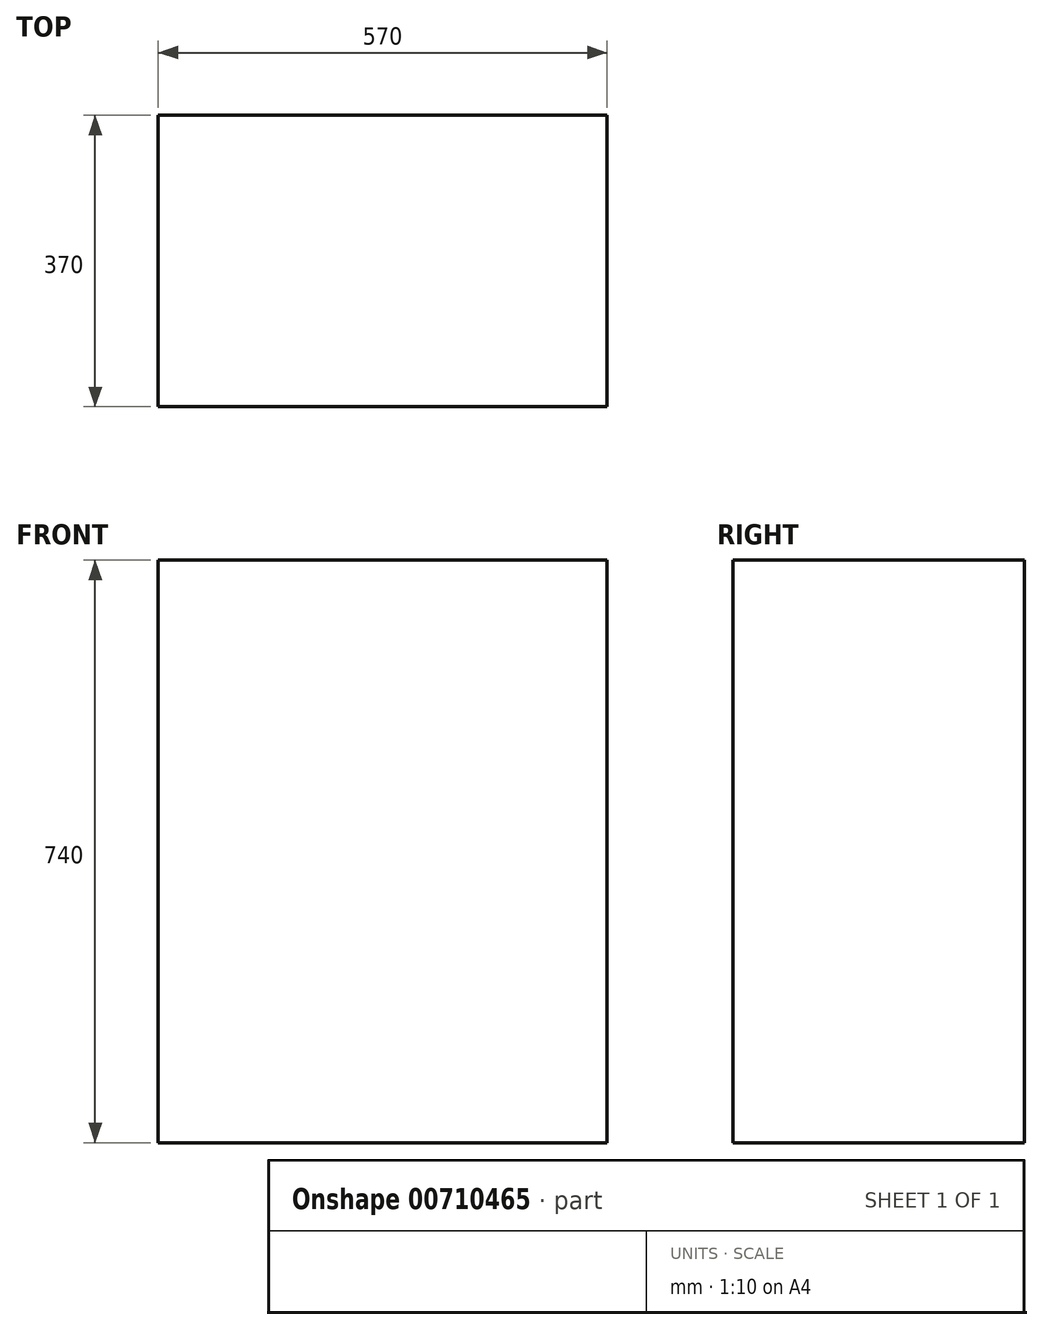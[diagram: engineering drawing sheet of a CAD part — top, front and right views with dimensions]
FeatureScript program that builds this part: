
annotation { "Feature Type Name" : "Feature", "Feature Type Description" : "" }
export const myFeature = defineFeature(function(context is Context, id is Id, definition is map)
    precondition{}
    {
        {
            var Q0;
            Q0=qCreatedBy(makeId("Top.planeOp"),FACE);
            var sketch = newSketch(context, id + "F0", { "sketchPlane" : qUnion([Q0])});
            skLineSegment(sketch, "E0.bottom", {"start": v(285, 185) * mm, "end": v(-285, 185) * mm});
            skLineSegment(sketch, "E0.top", {"start": v(285, -185) * mm, "end": v(-285, -185) * mm});
            skLineSegment(sketch, "E0.left", {"start": v(285, 185) * mm, "end": v(285, -185) * mm});
            skLineSegment(sketch, "E0.right", {"start": v(-285, 185) * mm, "end": v(-285, -185) * mm});
            skPoint(sketch, "E0.middle", {"position": v(0, 0) * mm});
            skSolve(sketch);
        }
        {
            var Q0;
            Q0=makeQuery(id+"F0.imprint","IMPRINT",FACE,{"disambiguationData":[TD([[makeQuery(id+"F0.imprint","IMPRINT",EDGE,{"derivedFrom":sQuery(id+"F0.wireOp",EDGE,"E0.bottom")}),1.0]])]});
            extrude(context, id + "F1", {"entities" : qUnion([Q0]), "depth" : 740 * mm, "offsetDistance" : 25 * mm});
        }
    });
